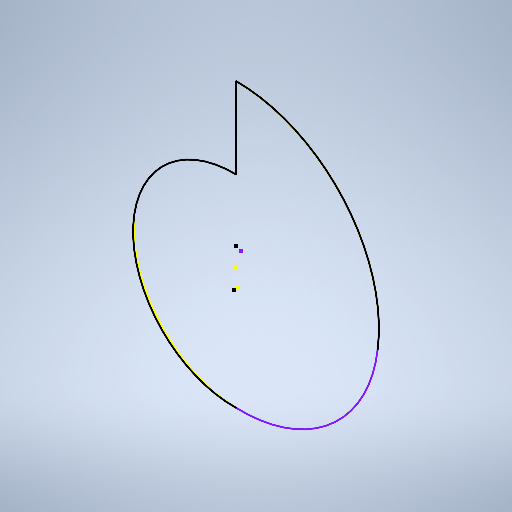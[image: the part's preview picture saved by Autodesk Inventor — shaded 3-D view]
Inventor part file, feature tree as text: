
AUTODESK INVENTOR PART (.ipt)
format: ipt  version: 2025 (Build 290162010, 162A)  size: 276,992 bytes
history: native  units: in
note: dims shown in document units (in); Inventor stores cm internally (conversion verified against a paired STEP export)
features: sketch x2, delete_face x2, extrude x1
ambient origin geometry x8: Origin, YZ Plane, XZ Plane, XY Plane, X Axis, Y Axis, Z Axis, Center Point
bodies: Solid1 (feature_tree)
feature tree (5):
  extrude  "Extrusion1"  Depth=0.5in
  sketch  "Sketch2"  dims[d4=0.25in d5=0.1875in d6=0.0in d7=0.5in d8=0.0344in d9=0.5in d10=0.0344in]
  delete_face  "Delete Face1"
  delete_face  "Delete Face2"
  sketch  "Sketch1"  dims[d1=1.0in d2=0.5in]
